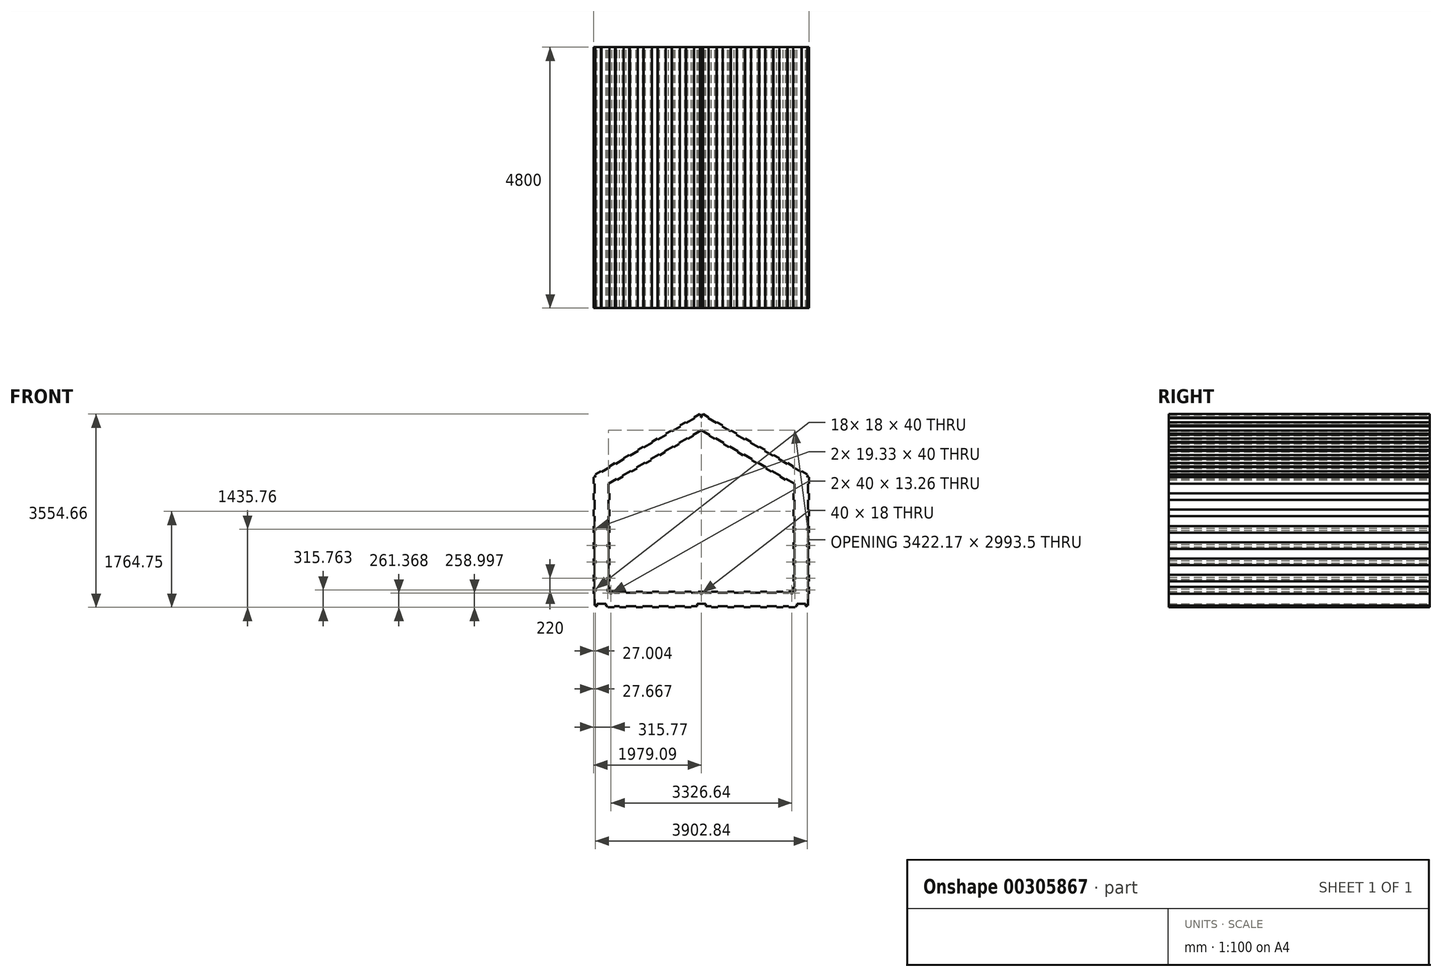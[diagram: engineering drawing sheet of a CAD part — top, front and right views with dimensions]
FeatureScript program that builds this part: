
annotation { "Feature Type Name" : "Feature", "Feature Type Description" : "" }
export const myFeature = defineFeature(function(context is Context, id is Id, definition is map)
    precondition{}
    {
        {
            var Q0;
            Q0=qCreatedBy(makeId("Front.planeOp"),FACE);
            var sketch = newSketch(context, id + "F0", { "sketchPlane" : qUnion([Q0])});
            skLineSegment(sketch, "E0", {"start": v(-89.77, -201.58) * mm, "end": v(-89.77, -291.34) * mm});
            skLineSegment(sketch, "E1", {"start": v(-89.77, -291.34) * mm, "end": v(0, -291.34) * mm});
            skLineSegment(sketch, "E2", {"start": v(0, -291.34) * mm, "end": v(0, -309.34) * mm});
            skLineSegment(sketch, "E3", {"start": v(0, -309.34) * mm, "end": v(100, -309.34) * mm});
            skLineSegment(sketch, "E4", {"start": v(100, -309.34) * mm, "end": v(100, -291.34) * mm});
            skLineSegment(sketch, "E5", {"start": v(100, -291.34) * mm, "end": v(220, -291.34) * mm});
            skLineSegment(sketch, "E6", {"start": v(220, -291.34) * mm, "end": v(220, -309.34) * mm});
            skLineSegment(sketch, "E7", {"start": v(220, -309.34) * mm, "end": v(400, -309.34) * mm});
            skLineSegment(sketch, "E8", {"start": v(400, -309.34) * mm, "end": v(400, -291.34) * mm});
            skLineSegment(sketch, "E9", {"start": v(400, -291.34) * mm, "end": v(520, -291.34) * mm});
            skLineSegment(sketch, "E10", {"start": v(520, -291.34) * mm, "end": v(520, -309.34) * mm});
            skLineSegment(sketch, "E11", {"start": v(520, -309.34) * mm, "end": v(700, -309.34) * mm});
            skLineSegment(sketch, "E12", {"start": v(700, -309.34) * mm, "end": v(700, -291.34) * mm});
            skLineSegment(sketch, "E13", {"start": v(700, -291.34) * mm, "end": v(820, -291.34) * mm});
            skLineSegment(sketch, "E14", {"start": v(820, -291.34) * mm, "end": v(820, -309.34) * mm});
            skLineSegment(sketch, "E15", {"start": v(820, -309.34) * mm, "end": v(1000, -309.34) * mm});
            skLineSegment(sketch, "E16", {"start": v(1000, -309.34) * mm, "end": v(1000, -291.34) * mm});
            skLineSegment(sketch, "E17", {"start": v(1000, -291.34) * mm, "end": v(1120, -291.34) * mm});
            skLineSegment(sketch, "E18", {"start": v(1120, -291.34) * mm, "end": v(1120, -309.34) * mm});
            skLineSegment(sketch, "E19", {"start": v(1120, -309.34) * mm, "end": v(1300, -309.34) * mm});
            skLineSegment(sketch, "E20", {"start": v(1300, -309.34) * mm, "end": v(1300, -291.34) * mm});
            skLineSegment(sketch, "E21", {"start": v(1300, -291.34) * mm, "end": v(1420, -291.34) * mm});
            skLineSegment(sketch, "E22", {"start": v(1420, -291.34) * mm, "end": v(1420, -309.34) * mm});
            skLineSegment(sketch, "E23", {"start": v(1420, -309.34) * mm, "end": v(1543.32, -309.34) * mm});
            skLineSegment(sketch, "E24", {"start": v(1543.32, -309.34) * mm, "end": v(1543.32, -291.34) * mm});
            skLineSegment(sketch, "E25", {"start": v(1543.32, -291.34) * mm, "end": v(1603.32, -291.34) * mm});
            skLineSegment(sketch, "E26.bottom", {"start": v(1583.32, -309.34) * mm, "end": v(1603.32, -309.34) * mm});
            skLineSegment(sketch, "E26.top", {"start": v(1583.32, -327.34) * mm, "end": v(1603.32, -327.34) * mm});
            skLineSegment(sketch, "E26.left", {"start": v(1583.32, -309.34) * mm, "end": v(1583.32, -327.34) * mm});
            skLineSegment(sketch, "E26.right", {"start": v(1603.32, -309.34) * mm, "end": v(1603.32, -327.34) * mm});
            skLineSegment(sketch, "E27", {"start": v(-89.77, -201.58) * mm, "end": v(-107.77, -201.58) * mm});
            skLineSegment(sketch, "E28", {"start": v(-107.77, -201.58) * mm, "end": v(-107.77, -101.58) * mm});
            skLineSegment(sketch, "E29", {"start": v(-107.77, -101.58) * mm, "end": v(-89.77, -101.58) * mm});
            skLineSegment(sketch, "E30", {"start": v(-89.77, -101.58) * mm, "end": v(-89.77, 18.42) * mm});
            skLineSegment(sketch, "E31", {"start": v(-89.77, 18.42) * mm, "end": v(-107.77, 18.42) * mm});
            skLineSegment(sketch, "E32", {"start": v(-107.77, 18.42) * mm, "end": v(-107.77, 198.42) * mm});
            skLineSegment(sketch, "E33", {"start": v(-107.77, 198.42) * mm, "end": v(-89.77, 198.42) * mm});
            skLineSegment(sketch, "E34", {"start": v(-89.77, 198.42) * mm, "end": v(-89.77, 318.42) * mm});
            skLineSegment(sketch, "E35", {"start": v(-89.77, 318.42) * mm, "end": v(-107.77, 318.42) * mm});
            skLineSegment(sketch, "E36", {"start": v(-107.77, 318.42) * mm, "end": v(-107.77, 498.42) * mm});
            skLineSegment(sketch, "E37.bottom", {"start": v(-107.77, -241.58) * mm, "end": v(-125.77, -241.58) * mm});
            skLineSegment(sketch, "E37.top", {"start": v(-107.77, -281.58) * mm, "end": v(-125.77, -281.58) * mm});
            skLineSegment(sketch, "E37.left", {"start": v(-107.77, -241.58) * mm, "end": v(-107.77, -281.58) * mm});
            skLineSegment(sketch, "E37.right", {"start": v(-125.77, -241.58) * mm, "end": v(-125.77, -281.58) * mm});
            skLineSegment(sketch, "E38.bottom", {"start": v(-40, -309.34) * mm, "end": v(-80, -309.34) * mm});
            skLineSegment(sketch, "E38.top", {"start": v(-40, -322.6) * mm, "end": v(-80, -322.6) * mm});
            skLineSegment(sketch, "E38.left", {"start": v(-40, -309.34) * mm, "end": v(-40, -322.6) * mm});
            skLineSegment(sketch, "E38.right", {"start": v(-80, -309.34) * mm, "end": v(-80, -322.6) * mm});
            skLineSegment(sketch, "E39", {"start": v(-107.77, -201.58) * mm, "end": v(-357.77, -201.58) * mm, "construction": true});
            skLineSegment(sketch, "E40", {"start": v(-357.77, -201.58) * mm, "end": v(-375.77, -201.58) * mm});
            skLineSegment(sketch, "E41", {"start": v(-375.77, -201.58) * mm, "end": v(-375.77, -327.35) * mm});
            skLineSegment(sketch, "E42", {"start": v(-357.77, -201.58) * mm, "end": v(-357.77, -101.58) * mm});
            skLineSegment(sketch, "E43", {"start": v(-357.77, -101.58) * mm, "end": v(-375.77, -101.58) * mm});
            skLineSegment(sketch, "E44.bottom", {"start": v(-357.77, -241.58) * mm, "end": v(-339.77, -241.58) * mm});
            skLineSegment(sketch, "E44.top", {"start": v(-357.77, -281.58) * mm, "end": v(-339.77, -281.58) * mm});
            skLineSegment(sketch, "E44.left", {"start": v(-357.77, -241.58) * mm, "end": v(-357.77, -281.58) * mm});
            skLineSegment(sketch, "E44.right", {"start": v(-339.77, -241.58) * mm, "end": v(-339.77, -281.58) * mm});
            skLineSegment(sketch, "E45", {"start": v(-375.77, -101.58) * mm, "end": v(-375.77, 18.42) * mm});
            skLineSegment(sketch, "E46", {"start": v(-375.77, 18.42) * mm, "end": v(-357.77, 18.42) * mm});
            skLineSegment(sketch, "E47.bottom", {"start": v(-357.77, -61.58) * mm, "end": v(-339.77, -61.58) * mm});
            skLineSegment(sketch, "E47.top", {"start": v(-357.77, -21.58) * mm, "end": v(-339.77, -21.58) * mm});
            skLineSegment(sketch, "E47.left", {"start": v(-357.77, -61.58) * mm, "end": v(-357.77, -21.58) * mm});
            skLineSegment(sketch, "E47.right", {"start": v(-339.77, -61.58) * mm, "end": v(-339.77, -21.58) * mm});
            skLineSegment(sketch, "E48", {"start": v(-357.77, 18.42) * mm, "end": v(-357.77, 198.42) * mm});
            skLineSegment(sketch, "E49", {"start": v(-357.77, 198.42) * mm, "end": v(-375.77, 198.42) * mm});
            skLineSegment(sketch, "E50.bottom", {"start": v(-107.77, -21.58) * mm, "end": v(-125.77, -21.58) * mm});
            skLineSegment(sketch, "E50.top", {"start": v(-107.77, -61.58) * mm, "end": v(-125.77, -61.58) * mm});
            skLineSegment(sketch, "E50.left", {"start": v(-107.77, -21.58) * mm, "end": v(-107.77, -61.58) * mm});
            skLineSegment(sketch, "E50.right", {"start": v(-125.77, -21.58) * mm, "end": v(-125.77, -61.58) * mm});
            skLineSegment(sketch, "E51", {"start": v(-375.77, 198.42) * mm, "end": v(-375.77, 318.42) * mm});
            skLineSegment(sketch, "E52", {"start": v(-375.77, 318.42) * mm, "end": v(-357.77, 318.42) * mm});
            skLineSegment(sketch, "E53", {"start": v(-357.77, 318.42) * mm, "end": v(-357.77, 498.42) * mm});
            skLineSegment(sketch, "E54.bottom", {"start": v(-357.77, 238.42) * mm, "end": v(-339.77, 238.42) * mm});
            skLineSegment(sketch, "E54.top", {"start": v(-357.77, 278.42) * mm, "end": v(-339.77, 278.42) * mm});
            skLineSegment(sketch, "E54.left", {"start": v(-357.77, 238.42) * mm, "end": v(-357.77, 278.42) * mm});
            skLineSegment(sketch, "E54.right", {"start": v(-339.77, 238.42) * mm, "end": v(-339.77, 278.42) * mm});
            skLineSegment(sketch, "E55.bottom", {"start": v(-107.77, 238.42) * mm, "end": v(-125.77, 238.42) * mm});
            skLineSegment(sketch, "E55.top", {"start": v(-107.77, 278.42) * mm, "end": v(-125.77, 278.42) * mm});
            skLineSegment(sketch, "E55.left", {"start": v(-107.77, 238.42) * mm, "end": v(-107.77, 278.42) * mm});
            skLineSegment(sketch, "E55.right", {"start": v(-125.77, 238.42) * mm, "end": v(-125.77, 278.42) * mm});
            skLineSegment(sketch, "E56", {"start": v(-357.77, 498.42) * mm, "end": v(-375.77, 498.42) * mm});
            skLineSegment(sketch, "E57", {"start": v(-375.77, 498.42) * mm, "end": v(-375.77, 618.42) * mm});
            skLineSegment(sketch, "E58", {"start": v(-107.77, 498.42) * mm, "end": v(-89.77, 498.42) * mm});
            skLineSegment(sketch, "E59", {"start": v(-89.77, 498.42) * mm, "end": v(-89.77, 618.42) * mm});
            skLineSegment(sketch, "E60.bottom", {"start": v(-357.77, 538.42) * mm, "end": v(-339.77, 538.42) * mm});
            skLineSegment(sketch, "E60.top", {"start": v(-357.77, 578.42) * mm, "end": v(-339.77, 578.42) * mm});
            skLineSegment(sketch, "E60.left", {"start": v(-357.77, 538.42) * mm, "end": v(-357.77, 578.42) * mm});
            skLineSegment(sketch, "E60.right", {"start": v(-339.77, 538.42) * mm, "end": v(-339.77, 578.42) * mm});
            skLineSegment(sketch, "E61.bottom", {"start": v(-107.77, 538.42) * mm, "end": v(-125.77, 538.42) * mm});
            skLineSegment(sketch, "E61.top", {"start": v(-107.77, 578.42) * mm, "end": v(-125.77, 578.42) * mm});
            skLineSegment(sketch, "E61.left", {"start": v(-107.77, 538.42) * mm, "end": v(-107.77, 578.42) * mm});
            skLineSegment(sketch, "E61.right", {"start": v(-125.77, 538.42) * mm, "end": v(-125.77, 578.42) * mm});
            skLineSegment(sketch, "E62", {"start": v(-375.77, 618.42) * mm, "end": v(-357.77, 618.42) * mm});
            skPoint(sketch, "E62.endSnap0", {"position": v(-357.77, 558.42) * mm});
            skLineSegment(sketch, "E63", {"start": v(-89.77, 618.42) * mm, "end": v(-107.77, 618.42) * mm});
            skPoint(sketch, "E63.endSnap0", {"position": v(-107.77, 558.42) * mm});
            skLineSegment(sketch, "E64", {"start": v(-357.77, 618.42) * mm, "end": v(-357.77, 798.42) * mm});
            skLineSegment(sketch, "E65", {"start": v(-107.77, 618.42) * mm, "end": v(-107.77, 798.42) * mm});
            skLineSegment(sketch, "E66", {"start": v(-107.77, 798.42) * mm, "end": v(-89.77, 798.42) * mm});
            skLineSegment(sketch, "E67", {"start": v(-89.77, 798.42) * mm, "end": v(-89.77, 918.42) * mm});
            skLineSegment(sketch, "E68", {"start": v(-89.77, 918.42) * mm, "end": v(-107.77, 918.42) * mm});
            skLineSegment(sketch, "E69", {"start": v(-107.77, 918.42) * mm, "end": v(-107.77, 1098.42) * mm});
            skLineSegment(sketch, "E70", {"start": v(-357.77, 798.42) * mm, "end": v(-375.77, 798.42) * mm});
            skLineSegment(sketch, "E71", {"start": v(-375.77, 798.42) * mm, "end": v(-375.77, 918.42) * mm});
            skLineSegment(sketch, "E72", {"start": v(-375.77, 918.42) * mm, "end": v(-357.77, 918.42) * mm});
            skLineSegment(sketch, "E73", {"start": v(-357.77, 918.42) * mm, "end": v(-357.77, 1098.42) * mm});
            skLineSegment(sketch, "E74.bottom", {"start": v(-357.77, 838.42) * mm, "end": v(-338.44, 838.42) * mm});
            skLineSegment(sketch, "E74.top", {"start": v(-357.77, 878.42) * mm, "end": v(-338.44, 878.42) * mm});
            skLineSegment(sketch, "E74.left", {"start": v(-357.77, 838.42) * mm, "end": v(-357.77, 878.42) * mm});
            skLineSegment(sketch, "E74.right", {"start": v(-338.44, 838.42) * mm, "end": v(-338.44, 878.42) * mm});
            skLineSegment(sketch, "E75.bottom", {"start": v(-107.77, 838.42) * mm, "end": v(-125.77, 838.42) * mm});
            skLineSegment(sketch, "E75.top", {"start": v(-107.77, 878.42) * mm, "end": v(-125.77, 878.42) * mm});
            skLineSegment(sketch, "E75.left", {"start": v(-107.77, 838.42) * mm, "end": v(-107.77, 878.42) * mm});
            skLineSegment(sketch, "E75.right", {"start": v(-125.77, 838.42) * mm, "end": v(-125.77, 878.42) * mm});
            skLineSegment(sketch, "E76", {"start": v(-357.77, 1098.42) * mm, "end": v(-375.77, 1098.42) * mm});
            skLineSegment(sketch, "E77", {"start": v(-375.77, 1098.42) * mm, "end": v(-375.77, 1218.42) * mm});
            skLineSegment(sketch, "E78", {"start": v(-107.77, 1098.42) * mm, "end": v(-89.77, 1098.42) * mm});
            skLineSegment(sketch, "E79", {"start": v(-89.77, 1098.42) * mm, "end": v(-89.77, 1218.42) * mm});
            skLineSegment(sketch, "E80", {"start": v(-375.77, 1218.42) * mm, "end": v(-357.77, 1218.42) * mm});
            skLineSegment(sketch, "E81", {"start": v(-357.77, 1218.42) * mm, "end": v(-357.77, 1398.42) * mm});
            skLineSegment(sketch, "E82", {"start": v(-89.77, 1218.42) * mm, "end": v(-107.77, 1218.42) * mm});
            skLineSegment(sketch, "E83", {"start": v(-107.77, 1218.42) * mm, "end": v(-107.77, 1398.42) * mm});
            skLineSegment(sketch, "E84", {"start": v(-357.77, 1398.42) * mm, "end": v(-375.77, 1398.42) * mm});
            skLineSegment(sketch, "E85", {"start": v(-375.77, 1398.42) * mm, "end": v(-375.77, 1518.42) * mm});
            skLineSegment(sketch, "E86", {"start": v(-375.77, 1518.42) * mm, "end": v(-357.77, 1518.42) * mm});
            skLineSegment(sketch, "E87", {"start": v(-107.77, 1398.42) * mm, "end": v(-89.77, 1398.42) * mm});
            skLineSegment(sketch, "E88", {"start": v(-89.77, 1398.42) * mm, "end": v(-89.77, 1518.42) * mm});
            skLineSegment(sketch, "E89", {"start": v(-89.77, 1518.42) * mm, "end": v(-107.77, 1518.42) * mm});
            skLineSegment(sketch, "E90", {"start": v(-357.77, 1518.42) * mm, "end": v(-357.77, 1698.42) * mm});
            skLineSegment(sketch, "E91", {"start": v(-357.77, 1698.42) * mm, "end": v(-375.77, 1698.42) * mm});
            skLineSegment(sketch, "E92", {"start": v(-375.77, 1698.42) * mm, "end": v(-375.77, 1818.42) * mm});
            skLineSegment(sketch, "E93", {"start": v(-375.77, 1818.42) * mm, "end": v(-357.77, 1818.42) * mm});
            skLineSegment(sketch, "E94", {"start": v(-357.77, 1818.42) * mm, "end": v(-357.77, 1840.65) * mm});
            skLineSegment(sketch, "E95", {"start": v(-357.77, 1818.42) * mm, "end": v(-338.51, 1851.77) * mm});
            skLineSegment(sketch, "E96", {"start": v(-357.77, 1840.65) * mm, "end": v(-338.51, 1851.77) * mm});
            skLineSegment(sketch, "E97", {"start": v(-338.51, 1851.77) * mm, "end": v(-347.51, 1867.36) * mm});
            skLineSegment(sketch, "E98", {"start": v(-347.51, 1867.36) * mm, "end": v(-243.59, 1927.35) * mm});
            skLineSegment(sketch, "E99", {"start": v(-243.59, 1927.35) * mm, "end": v(-234.59, 1911.77) * mm});
            skLineSegment(sketch, "E100", {"start": v(-234.59, 1911.77) * mm, "end": v(-78.7, 2001.76) * mm});
            skLineSegment(sketch, "E101", {"start": v(-78.7, 2001.76) * mm, "end": v(-87.7, 2017.35) * mm});
            skLineSegment(sketch, "E102", {"start": v(-87.7, 2017.35) * mm, "end": v(16.22, 2077.35) * mm});
            skLineSegment(sketch, "E103", {"start": v(16.22, 2077.35) * mm, "end": v(25.22, 2061.76) * mm});
            skLineSegment(sketch, "E104", {"start": v(-78.7, 2001.76) * mm, "end": v(46.3, 1785.25) * mm, "construction": true});
            skLineSegment(sketch, "E105", {"start": v(46.3, 1785.25) * mm, "end": v(55.3, 1769.67) * mm});
            skLineSegment(sketch, "E106", {"start": v(55.3, 1769.67) * mm, "end": v(159.22, 1829.66) * mm});
            skLineSegment(sketch, "E107", {"start": v(159.22, 1829.66) * mm, "end": v(150.22, 1845.25) * mm});
            skLineSegment(sketch, "E108", {"start": v(-107.77, 1518.42) * mm, "end": v(-107.77, 1696.31) * mm});
            skLineSegment(sketch, "E109", {"start": v(46.3, 1785.25) * mm, "end": v(-107.77, 1696.31) * mm});
            skLineSegment(sketch, "E110", {"start": v(25.22, 2061.76) * mm, "end": v(181.1, 2151.76) * mm});
            skLineSegment(sketch, "E111", {"start": v(150.22, 1845.25) * mm, "end": v(306.1, 1935.25) * mm});
            skLineSegment(sketch, "E112", {"start": v(181.1, 2151.76) * mm, "end": v(172.11, 2167.35) * mm});
            skLineSegment(sketch, "E113", {"start": v(172.11, 2167.35) * mm, "end": v(276.03, 2227.34) * mm});
            skLineSegment(sketch, "E114", {"start": v(306.1, 1935.25) * mm, "end": v(315.1, 1919.66) * mm});
            skLineSegment(sketch, "E115", {"start": v(315.1, 1919.66) * mm, "end": v(419.03, 1979.66) * mm});
            skLineSegment(sketch, "E116", {"start": v(419.03, 1979.66) * mm, "end": v(410.03, 1995.25) * mm});
            skLineSegment(sketch, "E117", {"start": v(410.03, 1995.25) * mm, "end": v(565.92, 2085.24) * mm});
            skLineSegment(sketch, "E118", {"start": v(276.03, 2227.34) * mm, "end": v(285.03, 2211.76) * mm});
            skLineSegment(sketch, "E119", {"start": v(285.03, 2211.76) * mm, "end": v(440.92, 2301.75) * mm});
            skLineSegment(sketch, "E120", {"start": v(440.92, 2301.75) * mm, "end": v(431.92, 2317.34) * mm});
            skLineSegment(sketch, "E121", {"start": v(431.92, 2317.34) * mm, "end": v(535.84, 2377.34) * mm});
            skLineSegment(sketch, "E122", {"start": v(565.92, 2085.24) * mm, "end": v(574.92, 2069.66) * mm});
            skLineSegment(sketch, "E123", {"start": v(574.92, 2069.66) * mm, "end": v(678.84, 2129.65) * mm});
            skLineSegment(sketch, "E124", {"start": v(535.84, 2377.34) * mm, "end": v(544.84, 2361.75) * mm});
            skLineSegment(sketch, "E125", {"start": v(544.84, 2361.75) * mm, "end": v(700.73, 2451.75) * mm});
            skLineSegment(sketch, "E126", {"start": v(678.84, 2129.65) * mm, "end": v(669.84, 2145.24) * mm});
            skLineSegment(sketch, "E127", {"start": v(669.84, 2145.24) * mm, "end": v(825.73, 2235.24) * mm});
            skLineSegment(sketch, "E128", {"start": v(700.73, 2451.75) * mm, "end": v(691.73, 2467.34) * mm});
            skLineSegment(sketch, "E129", {"start": v(691.73, 2467.34) * mm, "end": v(795.66, 2527.33) * mm});
            skLineSegment(sketch, "E130", {"start": v(825.73, 2235.24) * mm, "end": v(834.73, 2219.65) * mm});
            skLineSegment(sketch, "E131", {"start": v(834.73, 2219.65) * mm, "end": v(938.65, 2279.65) * mm});
            skLineSegment(sketch, "E132", {"start": v(795.66, 2527.33) * mm, "end": v(804.66, 2511.75) * mm});
            skLineSegment(sketch, "E133", {"start": v(804.66, 2511.75) * mm, "end": v(960.54, 2601.74) * mm});
            skLineSegment(sketch, "E134", {"start": v(960.54, 2601.74) * mm, "end": v(951.54, 2617.33) * mm});
            skLineSegment(sketch, "E135", {"start": v(951.54, 2617.33) * mm, "end": v(1055.47, 2677.33) * mm});
            skLineSegment(sketch, "E136", {"start": v(1055.47, 2677.33) * mm, "end": v(1064.47, 2661.74) * mm});
            skLineSegment(sketch, "E137", {"start": v(1064.47, 2661.74) * mm, "end": v(1220.35, 2751.74) * mm});
            skLineSegment(sketch, "E138", {"start": v(1220.35, 2751.74) * mm, "end": v(1211.35, 2767.33) * mm});
            skLineSegment(sketch, "E139", {"start": v(1211.35, 2767.33) * mm, "end": v(1315.28, 2827.32) * mm});
            skLineSegment(sketch, "E140", {"start": v(1315.28, 2827.32) * mm, "end": v(1324.28, 2811.74) * mm});
            skLineSegment(sketch, "E141", {"start": v(1324.28, 2811.74) * mm, "end": v(1480.16, 2901.73) * mm});
            skLineSegment(sketch, "E142", {"start": v(1480.16, 2901.73) * mm, "end": v(1471.16, 2917.32) * mm});
            skLineSegment(sketch, "E143", {"start": v(1471.16, 2917.32) * mm, "end": v(1575.09, 2977.32) * mm});
            skLineSegment(sketch, "E144", {"start": v(938.65, 2279.65) * mm, "end": v(929.65, 2295.24) * mm});
            skLineSegment(sketch, "E145", {"start": v(929.65, 2295.24) * mm, "end": v(1085.54, 2385.23) * mm});
            skLineSegment(sketch, "E146", {"start": v(1085.54, 2385.23) * mm, "end": v(1094.54, 2369.64) * mm});
            skLineSegment(sketch, "E147", {"start": v(1094.54, 2369.64) * mm, "end": v(1198.46, 2429.64) * mm});
            skLineSegment(sketch, "E148", {"start": v(1198.46, 2429.64) * mm, "end": v(1189.46, 2445.23) * mm});
            skLineSegment(sketch, "E149", {"start": v(1189.46, 2445.23) * mm, "end": v(1345.35, 2535.23) * mm});
            skLineSegment(sketch, "E150", {"start": v(1345.35, 2535.23) * mm, "end": v(1354.35, 2519.64) * mm});
            skLineSegment(sketch, "E151", {"start": v(1354.35, 2519.64) * mm, "end": v(1458.27, 2579.64) * mm});
            skLineSegment(sketch, "E152", {"start": v(1458.27, 2579.64) * mm, "end": v(1449.27, 2595.23) * mm});
            skLineSegment(sketch, "E153", {"start": v(1449.27, 2595.23) * mm, "end": v(1603.33, 2684.17) * mm});
            skLineSegment(sketch, "E154", {"start": v(1575.09, 2977.32) * mm, "end": v(1584.09, 2961.73) * mm});
            skLineSegment(sketch, "E155", {"start": v(1584.09, 2961.73) * mm, "end": v(1594.33, 2967.65) * mm});
            skLineSegment(sketch, "E156", {"start": v(1594.33, 2967.65) * mm, "end": v(1594.33, 2917.65) * mm});
            skLineSegment(sketch, "E157", {"start": v(1594.33, 2917.65) * mm, "end": v(1603.33, 2917.65) * mm});
            skLineSegment(sketch, "E158", {"start": v(960.54, 2601.74) * mm, "end": v(1085.54, 2385.23) * mm, "construction": true});
            skLineSegment(sketch, "E159", {"start": v(1420, -559.34) * mm, "end": v(1420, -577.34) * mm});
            skLineSegment(sketch, "E160", {"start": v(1420, -577.34) * mm, "end": v(1300, -577.34) * mm});
            skLineSegment(sketch, "E161", {"start": v(1300, -577.34) * mm, "end": v(1300, -559.34) * mm});
            skLineSegment(sketch, "E162", {"start": v(1300, -559.34) * mm, "end": v(1120, -559.34) * mm});
            skLineSegment(sketch, "E163", {"start": v(1120, -559.34) * mm, "end": v(1120, -577.34) * mm});
            skLineSegment(sketch, "E164", {"start": v(1120, -577.34) * mm, "end": v(1000, -577.34) * mm});
            skLineSegment(sketch, "E165", {"start": v(1000, -577.34) * mm, "end": v(1000, -559.34) * mm});
            skLineSegment(sketch, "E166", {"start": v(1000, -559.34) * mm, "end": v(820, -559.34) * mm});
            skLineSegment(sketch, "E167", {"start": v(820, -559.34) * mm, "end": v(820, -577.34) * mm});
            skLineSegment(sketch, "E168", {"start": v(820, -577.34) * mm, "end": v(700, -577.34) * mm});
            skLineSegment(sketch, "E169", {"start": v(700, -577.34) * mm, "end": v(700, -559.34) * mm});
            skLineSegment(sketch, "E170", {"start": v(700, -559.34) * mm, "end": v(520, -559.34) * mm});
            skLineSegment(sketch, "E171", {"start": v(520, -559.34) * mm, "end": v(520, -577.34) * mm});
            skLineSegment(sketch, "E172", {"start": v(520, -577.34) * mm, "end": v(400, -577.34) * mm});
            skLineSegment(sketch, "E173", {"start": v(400, -577.34) * mm, "end": v(400, -559.34) * mm});
            skLineSegment(sketch, "E174", {"start": v(400, -559.34) * mm, "end": v(220, -559.34) * mm});
            skLineSegment(sketch, "E175", {"start": v(220, -559.34) * mm, "end": v(220, -577.34) * mm});
            skLineSegment(sketch, "E176", {"start": v(220, -577.34) * mm, "end": v(100, -577.34) * mm});
            skLineSegment(sketch, "E177", {"start": v(100, -577.34) * mm, "end": v(100, -559.34) * mm});
            skLineSegment(sketch, "E178", {"start": v(100, -559.34) * mm, "end": v(0, -559.34) * mm});
            skLineSegment(sketch, "E179", {"start": v(0, -559.34) * mm, "end": v(0, -577.34) * mm});
            skLineSegment(sketch, "E180", {"start": v(0, -577.34) * mm, "end": v(-120, -577.34) * mm});
            skLineSegment(sketch, "E181", {"start": v(-120, -577.34) * mm, "end": v(-120, -559.34) * mm});
            skLineSegment(sketch, "E182", {"start": v(-120, -559.34) * mm, "end": v(-152.77, -559.34) * mm});
            skLineSegment(sketch, "E183", {"start": v(-152.77, -559.34) * mm, "end": v(-152.77, -509.34) * mm});
            skLineSegment(sketch, "E184", {"start": v(-152.77, -509.34) * mm, "end": v(-312.77, -509.34) * mm});
            skLineSegment(sketch, "E185", {"start": v(-312.77, -509.34) * mm, "end": v(-312.77, -559.34) * mm});
            skLineSegment(sketch, "E186", {"start": v(-312.77, -559.34) * mm, "end": v(-337.77, -559.34) * mm});
            skLineSegment(sketch, "E187", {"start": v(-337.77, -559.34) * mm, "end": v(-337.77, -541.34) * mm});
            skLineSegment(sketch, "E188", {"start": v(-337.77, -541.34) * mm, "end": v(-357.77, -541.34) * mm});
            skLineSegment(sketch, "E189", {"start": v(-357.77, -541.34) * mm, "end": v(-357.77, -327.35) * mm});
            skLineSegment(sketch, "E190", {"start": v(-357.77, -327.35) * mm, "end": v(-375.77, -327.35) * mm});
            skLineSegment(sketch, "E191", {"start": v(1603.32, -816.57) * mm, "end": v(1603.32, 3183.43) * mm, "construction": true});
            skLineSegment(sketch, "E192", {"start": v(1420, -559.34) * mm, "end": v(1523.32, -559.34) * mm});
            skLineSegment(sketch, "E193", {"start": v(1523.32, -559.34) * mm, "end": v(1523.32, -509.34) * mm});
            skLineSegment(sketch, "E194", {"start": v(1523.32, -509.34) * mm, "end": v(1603.32, -509.34) * mm});
            skLineSegment(sketch, "E195.MirrorCS", {"start": v(3564.4, 578.42) * mm, "end": v(3546.4, 578.42) * mm});
            skLineSegment(sketch, "E196.MirrorCS", {"start": v(3564.4, 1840.65) * mm, "end": v(3545.15, 1851.77) * mm});
            skLineSegment(sketch, "E197.MirrorCS", {"start": v(3564.4, 538.42) * mm, "end": v(3546.4, 538.42) * mm});
            skLineSegment(sketch, "E198.MirrorCS", {"start": v(3314.4, 578.42) * mm, "end": v(3332.4, 578.42) * mm});
            skLineSegment(sketch, "E199.MirrorCS", {"start": v(3582.4, 1818.42) * mm, "end": v(3564.4, 1818.42) * mm});
            skLineSegment(sketch, "E200.MirrorCS", {"start": v(3314.4, 538.42) * mm, "end": v(3332.4, 538.42) * mm});
            skLineSegment(sketch, "E201.MirrorCS", {"start": v(3564.4, 498.42) * mm, "end": v(3582.4, 498.42) * mm});
            skLineSegment(sketch, "E202.MirrorCS", {"start": v(3564.4, 538.42) * mm, "end": v(3564.4, 578.42) * mm});
            skLineSegment(sketch, "E203.MirrorCS", {"start": v(3545.15, 1851.77) * mm, "end": v(3554.15, 1867.36) * mm});
            skLineSegment(sketch, "E204.MirrorCS", {"start": v(3582.4, 618.42) * mm, "end": v(3564.4, 618.42) * mm});
            skLineSegment(sketch, "E205.MirrorCS", {"start": v(3564.4, -61.58) * mm, "end": v(3546.4, -61.58) * mm});
            skLineSegment(sketch, "E206.MirrorCS", {"start": v(3582.4, 498.42) * mm, "end": v(3582.4, 618.42) * mm});
            skLineSegment(sketch, "E207.MirrorCS", {"start": v(1663.32, -309.34) * mm, "end": v(1663.32, -291.34) * mm});
            skLineSegment(sketch, "E208.MirrorCS", {"start": v(3450.22, 1927.35) * mm, "end": v(3441.22, 1911.77) * mm});
            skLineSegment(sketch, "E209.MirrorCS", {"start": v(3546.4, 538.42) * mm, "end": v(3546.4, 578.42) * mm});
            skLineSegment(sketch, "E210.MirrorCS", {"start": v(3314.4, 498.42) * mm, "end": v(3296.4, 498.42) * mm});
            skLineSegment(sketch, "E211.MirrorCS", {"start": v(3554.15, 1867.36) * mm, "end": v(3450.22, 1927.35) * mm});
            skLineSegment(sketch, "E212.MirrorCS", {"start": v(3564.4, -281.58) * mm, "end": v(3546.4, -281.58) * mm});
            skLineSegment(sketch, "E213.MirrorCS", {"start": v(3564.4, -241.58) * mm, "end": v(3546.4, -241.58) * mm});
            skLineSegment(sketch, "E214.MirrorCS", {"start": v(3564.4, -21.58) * mm, "end": v(3546.4, -21.58) * mm});
            skLineSegment(sketch, "E215.MirrorCS", {"start": v(3296.4, 618.42) * mm, "end": v(3314.4, 618.42) * mm});
            skLineSegment(sketch, "E216.MirrorCS", {"start": v(3564.4, -61.58) * mm, "end": v(3564.4, -21.58) * mm});
            skLineSegment(sketch, "E217.MirrorCS", {"start": v(3332.4, 538.42) * mm, "end": v(3332.4, 578.42) * mm});
            skLineSegment(sketch, "E218.MirrorCS", {"start": v(1623.32, -327.34) * mm, "end": v(1603.32, -327.34) * mm});
            skLineSegment(sketch, "E219.MirrorCS", {"start": v(3564.4, 1818.42) * mm, "end": v(3564.4, 1840.65) * mm});
            skLineSegment(sketch, "E220.MirrorCS", {"start": v(3564.4, 1818.42) * mm, "end": v(3545.15, 1851.77) * mm});
            skLineSegment(sketch, "E221.MirrorCS", {"start": v(3296.4, 498.42) * mm, "end": v(3296.4, 618.42) * mm});
            skLineSegment(sketch, "E222.MirrorCS", {"start": v(3314.4, 538.42) * mm, "end": v(3314.4, 578.42) * mm});
            skLineSegment(sketch, "E223.MirrorCS", {"start": v(1623.32, -309.34) * mm, "end": v(1603.32, -309.34) * mm});
            skLineSegment(sketch, "E224.MirrorCS", {"start": v(3564.4, 278.42) * mm, "end": v(3546.4, 278.42) * mm});
            skLineSegment(sketch, "E225.MirrorCS", {"start": v(3564.4, 878.42) * mm, "end": v(3545.08, 878.42) * mm});
            skLineSegment(sketch, "E226.MirrorCS", {"start": v(1663.32, -291.34) * mm, "end": v(1603.32, -291.34) * mm});
            skLineSegment(sketch, "E227.MirrorCS", {"start": v(3314.4, -281.58) * mm, "end": v(3332.4, -281.58) * mm});
            skLineSegment(sketch, "E228.MirrorCS", {"start": v(3582.4, -101.58) * mm, "end": v(3582.4, 18.42) * mm});
            skLineSegment(sketch, "E229.MirrorCS", {"start": v(3564.4, -201.58) * mm, "end": v(3582.4, -201.58) * mm});
            skLineSegment(sketch, "E230.MirrorCS", {"start": v(3564.4, 238.42) * mm, "end": v(3546.4, 238.42) * mm});
            skLineSegment(sketch, "E231.MirrorCS", {"start": v(3564.4, 838.42) * mm, "end": v(3545.08, 838.42) * mm});
            skLineSegment(sketch, "E232.MirrorCS", {"start": v(3314.4, -241.58) * mm, "end": v(3332.4, -241.58) * mm});
            skLineSegment(sketch, "E233.MirrorCS", {"start": v(3564.4, -241.58) * mm, "end": v(3564.4, -281.58) * mm});
            skLineSegment(sketch, "E234.MirrorCS", {"start": v(3286.64, -309.34) * mm, "end": v(3286.64, -322.6) * mm});
            skLineSegment(sketch, "E235.MirrorCS", {"start": v(3296.4, -201.58) * mm, "end": v(3314.4, -201.58) * mm});
            skLineSegment(sketch, "E236.MirrorCS", {"start": v(3546.4, -61.58) * mm, "end": v(3546.4, -21.58) * mm});
            skLineSegment(sketch, "E237.MirrorCS", {"start": v(1623.32, -309.34) * mm, "end": v(1623.32, -327.34) * mm});
            skLineSegment(sketch, "E238.MirrorCS", {"start": v(3246.64, -322.6) * mm, "end": v(3286.64, -322.6) * mm});
            skLineSegment(sketch, "E239.MirrorCS", {"start": v(3332.4, -21.58) * mm, "end": v(3332.4, -61.58) * mm});
            skLineSegment(sketch, "E240.MirrorCS", {"start": v(3564.4, -101.58) * mm, "end": v(3582.4, -101.58) * mm});
            skLineSegment(sketch, "E241.MirrorCS", {"start": v(3564.4, -201.58) * mm, "end": v(3564.4, -101.58) * mm});
            skLineSegment(sketch, "E242.MirrorCS", {"start": v(3314.4, -21.58) * mm, "end": v(3314.4, -61.58) * mm});
            skLineSegment(sketch, "E243.MirrorCS", {"start": v(3582.4, 18.42) * mm, "end": v(3564.4, 18.42) * mm});
            skLineSegment(sketch, "E244.MirrorCS", {"start": v(3296.4, 18.42) * mm, "end": v(3314.4, 18.42) * mm});
            skLineSegment(sketch, "E245.MirrorCS", {"start": v(3564.4, -327.35) * mm, "end": v(3582.4, -327.35) * mm});
            skLineSegment(sketch, "E246.MirrorCS", {"start": v(3296.4, -101.58) * mm, "end": v(3296.4, 18.42) * mm});
            skLineSegment(sketch, "E247.MirrorCS", {"start": v(3314.4, -21.58) * mm, "end": v(3332.4, -21.58) * mm});
            skLineSegment(sketch, "E248.MirrorCS", {"start": v(3314.4, -101.58) * mm, "end": v(3296.4, -101.58) * mm});
            skLineSegment(sketch, "E249.MirrorCS", {"start": v(3546.4, -241.58) * mm, "end": v(3546.4, -281.58) * mm});
            skLineSegment(sketch, "E250.MirrorCS", {"start": v(3314.4, -201.58) * mm, "end": v(3564.4, -201.58) * mm, "construction": true});
            skLineSegment(sketch, "E251.MirrorCS", {"start": v(3314.4, -61.58) * mm, "end": v(3332.4, -61.58) * mm});
            skLineSegment(sketch, "E252.MirrorCS", {"start": v(3206.64, -291.34) * mm, "end": v(3206.64, -309.34) * mm});
            skLineSegment(sketch, "E253.MirrorCS", {"start": v(3296.4, -291.34) * mm, "end": v(3206.64, -291.34) * mm});
            skLineSegment(sketch, "E254.MirrorCS", {"start": v(3296.4, -201.58) * mm, "end": v(3296.4, -291.34) * mm});
            skLineSegment(sketch, "E255.MirrorCS", {"start": v(3314.4, -201.58) * mm, "end": v(3314.4, -101.58) * mm});
            skLineSegment(sketch, "E256.MirrorCS", {"start": v(3582.4, 318.42) * mm, "end": v(3564.4, 318.42) * mm});
            skLineSegment(sketch, "E257.MirrorCS", {"start": v(3246.64, -309.34) * mm, "end": v(3246.64, -322.6) * mm});
            skLineSegment(sketch, "E258.MirrorCS", {"start": v(3314.4, 838.42) * mm, "end": v(3332.4, 838.42) * mm});
            skLineSegment(sketch, "E259.MirrorCS", {"start": v(3246.64, -309.34) * mm, "end": v(3286.64, -309.34) * mm});
            skLineSegment(sketch, "E260.MirrorCS", {"start": v(3314.4, 878.42) * mm, "end": v(3332.4, 878.42) * mm});
            skLineSegment(sketch, "E261.MirrorCS", {"start": v(3564.4, 798.42) * mm, "end": v(3582.4, 798.42) * mm});
            skLineSegment(sketch, "E262.MirrorCS", {"start": v(3332.4, -241.58) * mm, "end": v(3332.4, -281.58) * mm});
            skLineSegment(sketch, "E263.MirrorCS", {"start": v(3564.4, 238.42) * mm, "end": v(3564.4, 278.42) * mm});
            skLineSegment(sketch, "E264.MirrorCS", {"start": v(3564.4, 838.42) * mm, "end": v(3564.4, 878.42) * mm});
            skLineSegment(sketch, "E265.MirrorCS", {"start": v(3314.4, -241.58) * mm, "end": v(3314.4, -281.58) * mm});
            skLineSegment(sketch, "E266.MirrorCS", {"start": v(3582.4, -201.58) * mm, "end": v(3582.4, -327.35) * mm});
            skLineSegment(sketch, "E267.MirrorCS", {"start": v(3296.4, 798.42) * mm, "end": v(3296.4, 918.42) * mm});
            skLineSegment(sketch, "E268.MirrorCS", {"start": v(3564.4, 198.42) * mm, "end": v(3582.4, 198.42) * mm});
            skLineSegment(sketch, "E269.MirrorCS", {"start": v(3564.4, 318.42) * mm, "end": v(3564.4, 498.42) * mm});
            skLineSegment(sketch, "E270.MirrorCS", {"start": v(3544.4, -541.34) * mm, "end": v(3564.4, -541.34) * mm});
            skLineSegment(sketch, "E271.MirrorCS", {"start": v(3314.4, 798.42) * mm, "end": v(3296.4, 798.42) * mm});
            skLineSegment(sketch, "E272.MirrorCS", {"start": v(3206.64, -309.34) * mm, "end": v(3106.64, -309.34) * mm});
            skLineSegment(sketch, "E273.MirrorCS", {"start": v(3314.4, 618.42) * mm, "end": v(3314.4, 798.42) * mm});
            skLineSegment(sketch, "E274.MirrorCS", {"start": v(3332.4, 838.42) * mm, "end": v(3332.4, 878.42) * mm});
            skLineSegment(sketch, "E275.MirrorCS", {"start": v(3564.4, 18.42) * mm, "end": v(3564.4, 198.42) * mm});
            skLineSegment(sketch, "E276.MirrorCS", {"start": v(3582.4, 918.42) * mm, "end": v(3564.4, 918.42) * mm});
            skLineSegment(sketch, "E277.MirrorCS", {"start": v(3296.4, 318.42) * mm, "end": v(3314.4, 318.42) * mm});
            skLineSegment(sketch, "E278.MirrorCS", {"start": v(1631.55, 2977.32) * mm, "end": v(1622.55, 2961.73) * mm});
            skLineSegment(sketch, "E279.MirrorCS", {"start": v(3564.4, 618.42) * mm, "end": v(3564.4, 798.42) * mm});
            skLineSegment(sketch, "E280.MirrorCS", {"start": v(3314.4, 838.42) * mm, "end": v(3314.4, 878.42) * mm});
            skLineSegment(sketch, "E281.MirrorCS", {"start": v(3582.4, 798.42) * mm, "end": v(3582.4, 918.42) * mm});
            skLineSegment(sketch, "E282.MirrorCS", {"start": v(3582.4, 198.42) * mm, "end": v(3582.4, 318.42) * mm});
            skLineSegment(sketch, "E283.MirrorCS", {"start": v(3314.4, 238.42) * mm, "end": v(3332.4, 238.42) * mm});
            skLineSegment(sketch, "E284.MirrorCS", {"start": v(3519.4, -509.34) * mm, "end": v(3519.4, -559.34) * mm});
            skLineSegment(sketch, "E285.MirrorCS", {"start": v(3314.4, 278.42) * mm, "end": v(3332.4, 278.42) * mm});
            skLineSegment(sketch, "E286.MirrorCS", {"start": v(3314.4, 198.42) * mm, "end": v(3296.4, 198.42) * mm});
            skLineSegment(sketch, "E287.MirrorCS", {"start": v(3546.4, 238.42) * mm, "end": v(3546.4, 278.42) * mm});
            skLineSegment(sketch, "E288.MirrorCS", {"start": v(3545.08, 838.42) * mm, "end": v(3545.08, 878.42) * mm});
            skLineSegment(sketch, "E289.MirrorCS", {"start": v(3296.4, 918.42) * mm, "end": v(3314.4, 918.42) * mm});
            skLineSegment(sketch, "E290.MirrorCS", {"start": v(3326.64, -559.34) * mm, "end": v(3359.4, -559.34) * mm});
            skLineSegment(sketch, "E291.MirrorCS", {"start": v(1726.47, 2901.73) * mm, "end": v(1735.47, 2917.32) * mm});
            skLineSegment(sketch, "E292.MirrorCS", {"start": v(3326.64, -577.34) * mm, "end": v(3326.64, -559.34) * mm});
            skLineSegment(sketch, "E293.MirrorCS", {"start": v(3285.34, 2001.76) * mm, "end": v(3294.34, 2017.35) * mm});
            skLineSegment(sketch, "E294.MirrorCS", {"start": v(3206.64, -577.34) * mm, "end": v(3326.64, -577.34) * mm});
            skLineSegment(sketch, "E295.MirrorCS", {"start": v(3564.4, -541.34) * mm, "end": v(3564.4, -327.35) * mm});
            skLineSegment(sketch, "E296.MirrorCS", {"start": v(1612.3, 2917.65) * mm, "end": v(1603.3, 2917.65) * mm});
            skLineSegment(sketch, "E297.MirrorCS", {"start": v(1612.3, 2967.65) * mm, "end": v(1612.3, 2917.65) * mm});
            skLineSegment(sketch, "E298.MirrorCS", {"start": v(3314.4, 318.42) * mm, "end": v(3314.4, 498.42) * mm});
            skLineSegment(sketch, "E299.MirrorCS", {"start": v(3106.64, -309.34) * mm, "end": v(3106.64, -291.34) * mm});
            skLineSegment(sketch, "E300.MirrorCS", {"start": v(3544.4, -559.34) * mm, "end": v(3544.4, -541.34) * mm});
            skLineSegment(sketch, "E301.MirrorCS", {"start": v(1622.55, 2961.73) * mm, "end": v(1612.3, 2967.65) * mm});
            skLineSegment(sketch, "E302.MirrorCS", {"start": v(3332.4, 238.42) * mm, "end": v(3332.4, 278.42) * mm});
            skLineSegment(sketch, "E303.MirrorCS", {"start": v(3519.4, -559.34) * mm, "end": v(3544.4, -559.34) * mm});
            skLineSegment(sketch, "E304.MirrorCS", {"start": v(2640.72, 2085.24) * mm, "end": v(2631.72, 2069.66) * mm});
            skLineSegment(sketch, "E305.MirrorCS", {"start": v(3314.4, 238.42) * mm, "end": v(3314.4, 278.42) * mm});
            skLineSegment(sketch, "E306.MirrorCS", {"start": v(3296.4, 198.42) * mm, "end": v(3296.4, 318.42) * mm});
            skLineSegment(sketch, "E307.MirrorCS", {"start": v(3359.4, -509.34) * mm, "end": v(3519.4, -509.34) * mm});
            skLineSegment(sketch, "E308.MirrorCS", {"start": v(3160.34, 1785.25) * mm, "end": v(3151.34, 1769.67) * mm});
            skLineSegment(sketch, "E309.MirrorCS", {"start": v(3359.4, -559.34) * mm, "end": v(3359.4, -509.34) * mm});
            skLineSegment(sketch, "E310.MirrorCS", {"start": v(1735.47, 2917.32) * mm, "end": v(1631.55, 2977.32) * mm});
            skLineSegment(sketch, "E311.MirrorCS", {"start": v(3314.4, 18.42) * mm, "end": v(3314.4, 198.42) * mm});
            skLineSegment(sketch, "E312.MirrorCS", {"start": v(2246.1, 2601.74) * mm, "end": v(2255.1, 2617.33) * mm});
            skLineSegment(sketch, "E313.MirrorCS", {"start": v(2527.8, 2129.65) * mm, "end": v(2536.8, 2145.24) * mm});
            skLineSegment(sketch, "E314.MirrorCS", {"start": v(3441.22, 1911.77) * mm, "end": v(3285.34, 2001.76) * mm});
            skLineSegment(sketch, "E315.MirrorCS", {"start": v(3206.64, -559.34) * mm, "end": v(3206.64, -577.34) * mm});
            skLineSegment(sketch, "E316.MirrorCS", {"start": v(2631.72, 2069.66) * mm, "end": v(2527.8, 2129.65) * mm});
            skLineSegment(sketch, "E317.MirrorCS", {"start": v(3047.42, 1829.66) * mm, "end": v(3056.42, 1845.25) * mm});
            skLineSegment(sketch, "E318.MirrorCS", {"start": v(2121.1, 2385.23) * mm, "end": v(2112.1, 2369.64) * mm});
            skLineSegment(sketch, "E319.MirrorCS", {"start": v(3106.64, -559.34) * mm, "end": v(3206.64, -559.34) * mm});
            skLineSegment(sketch, "E320.MirrorCS", {"start": v(3151.34, 1769.67) * mm, "end": v(3047.42, 1829.66) * mm});
            skLineSegment(sketch, "E321.MirrorCS", {"start": v(3106.64, -577.34) * mm, "end": v(3106.64, -559.34) * mm});
            skLineSegment(sketch, "E322.MirrorCS", {"start": v(3285.34, 2001.76) * mm, "end": v(3160.34, 1785.25) * mm, "construction": true});
            skLineSegment(sketch, "E323.MirrorCS", {"start": v(2151.17, 2677.33) * mm, "end": v(2142.17, 2661.74) * mm});
            skLineSegment(sketch, "E324.MirrorCS", {"start": v(2506.64, -577.34) * mm, "end": v(2506.64, -559.34) * mm});
            skLineSegment(sketch, "E325.MirrorCS", {"start": v(2505.9, 2451.75) * mm, "end": v(2514.9, 2467.34) * mm});
            skLineSegment(sketch, "E326.MirrorCS", {"start": v(2267.99, 2279.65) * mm, "end": v(2276.99, 2295.24) * mm});
            skLineSegment(sketch, "E327.MirrorCS", {"start": v(3025.53, 2151.76) * mm, "end": v(3034.53, 2167.35) * mm});
            skLineSegment(sketch, "E328.MirrorCS", {"start": v(2386.64, -559.34) * mm, "end": v(2386.64, -577.34) * mm});
            skLineSegment(sketch, "E329.MirrorCS", {"start": v(3190.41, 2077.35) * mm, "end": v(3181.41, 2061.76) * mm});
            skLineSegment(sketch, "E330.MirrorCS", {"start": v(2255.1, 2617.33) * mm, "end": v(2151.17, 2677.33) * mm});
            skLineSegment(sketch, "E331.MirrorCS", {"start": v(2536.8, 2145.24) * mm, "end": v(2380.9, 2235.24) * mm});
            skLineSegment(sketch, "E332.MirrorCS", {"start": v(1786.64, -559.34) * mm, "end": v(1786.64, -577.34) * mm});
            skLineSegment(sketch, "E333.MirrorCS", {"start": v(3294.34, 2017.35) * mm, "end": v(3190.41, 2077.35) * mm});
            skLineSegment(sketch, "E334.MirrorCS", {"start": v(1861.29, 2535.23) * mm, "end": v(1852.29, 2519.64) * mm});
            skLineSegment(sketch, "E335.MirrorCS", {"start": v(2206.64, -577.34) * mm, "end": v(2206.64, -559.34) * mm});
            skLineSegment(sketch, "E336.MirrorCS", {"start": v(2401.98, 2511.75) * mm, "end": v(2246.1, 2601.74) * mm});
            skLineSegment(sketch, "E337.MirrorCS", {"start": v(2017.17, 2445.23) * mm, "end": v(1861.29, 2535.23) * mm});
            skLineSegment(sketch, "E338.MirrorCS", {"start": v(2787.6, 1979.66) * mm, "end": v(2796.6, 1995.25) * mm});
            skLineSegment(sketch, "E339.MirrorCS", {"start": v(2661.8, 2361.75) * mm, "end": v(2505.9, 2451.75) * mm});
            skLineSegment(sketch, "E340.MirrorCS", {"start": v(2008.17, 2429.64) * mm, "end": v(2017.17, 2445.23) * mm});
            skLineSegment(sketch, "E341.MirrorCS", {"start": v(2410.98, 2527.33) * mm, "end": v(2401.98, 2511.75) * mm});
            skLineSegment(sketch, "E342.MirrorCS", {"start": v(2086.64, -559.34) * mm, "end": v(2086.64, -577.34) * mm});
            skLineSegment(sketch, "E343.MirrorCS", {"start": v(2891.53, 1919.66) * mm, "end": v(2787.6, 1979.66) * mm});
            skLineSegment(sketch, "E344.MirrorCS", {"start": v(2371.9, 2219.65) * mm, "end": v(2267.99, 2279.65) * mm});
            skLineSegment(sketch, "E345.MirrorCS", {"start": v(2112.1, 2369.64) * mm, "end": v(2008.17, 2429.64) * mm});
            skLineSegment(sketch, "E346.MirrorCS", {"start": v(2670.8, 2377.34) * mm, "end": v(2661.8, 2361.75) * mm});
            skLineSegment(sketch, "E347.MirrorCS", {"start": v(2506.64, -309.34) * mm, "end": v(2506.64, -291.34) * mm});
            skLineSegment(sketch, "E348.MirrorCS", {"start": v(3106.64, -291.34) * mm, "end": v(2986.64, -291.34) * mm});
            skLineSegment(sketch, "E349.MirrorCS", {"start": v(2386.64, -291.34) * mm, "end": v(2386.64, -309.34) * mm});
            skLineSegment(sketch, "E350.MirrorCS", {"start": v(2506.64, -291.34) * mm, "end": v(2386.64, -291.34) * mm});
            skLineSegment(sketch, "E351.MirrorCS", {"start": v(2380.9, 2235.24) * mm, "end": v(2371.9, 2219.65) * mm});
            skLineSegment(sketch, "E352.MirrorCS", {"start": v(2900.53, 1935.25) * mm, "end": v(2891.53, 1919.66) * mm});
            skLineSegment(sketch, "E353.MirrorCS", {"start": v(1786.64, -291.34) * mm, "end": v(1786.64, -309.34) * mm});
            skLineSegment(sketch, "E354.MirrorCS", {"start": v(1683.32, -559.34) * mm, "end": v(1683.32, -509.34) * mm});
            skLineSegment(sketch, "E355.MirrorCS", {"start": v(2514.9, 2467.34) * mm, "end": v(2410.98, 2527.33) * mm});
            skLineSegment(sketch, "E356.MirrorCS", {"start": v(2276.99, 2295.24) * mm, "end": v(2121.1, 2385.23) * mm});
            skLineSegment(sketch, "E357.MirrorCS", {"start": v(3034.53, 2167.35) * mm, "end": v(2930.6, 2227.34) * mm});
            skLineSegment(sketch, "E358.MirrorCS", {"start": v(2386.64, -577.34) * mm, "end": v(2506.64, -577.34) * mm});
            skLineSegment(sketch, "E359.MirrorCS", {"start": v(2765.72, 2301.75) * mm, "end": v(2774.72, 2317.34) * mm});
            skLineSegment(sketch, "E360.MirrorCS", {"start": v(1748.36, 2579.64) * mm, "end": v(1757.36, 2595.23) * mm});
            skLineSegment(sketch, "E361.MirrorCS", {"start": v(1906.64, -291.34) * mm, "end": v(1786.64, -291.34) * mm});
            skLineSegment(sketch, "E362.MirrorCS", {"start": v(2774.72, 2317.34) * mm, "end": v(2670.8, 2377.34) * mm});
            skLineSegment(sketch, "E363.MirrorCS", {"start": v(1786.64, -559.34) * mm, "end": v(1683.32, -559.34) * mm});
            skLineSegment(sketch, "E364.MirrorCS", {"start": v(1786.64, -577.34) * mm, "end": v(1906.64, -577.34) * mm});
            skLineSegment(sketch, "E365.MirrorCS", {"start": v(2921.6, 2211.76) * mm, "end": v(2765.72, 2301.75) * mm});
            skLineSegment(sketch, "E366.MirrorCS", {"start": v(1906.64, -309.34) * mm, "end": v(1906.64, -291.34) * mm});
            skLineSegment(sketch, "E367.MirrorCS", {"start": v(1852.29, 2519.64) * mm, "end": v(1748.36, 2579.64) * mm});
            skLineSegment(sketch, "E368.MirrorCS", {"start": v(2986.64, -559.34) * mm, "end": v(2986.64, -577.34) * mm});
            skLineSegment(sketch, "E369.MirrorCS", {"start": v(3056.42, 1845.25) * mm, "end": v(2900.53, 1935.25) * mm});
            skLineSegment(sketch, "E370.MirrorCS", {"start": v(2930.6, 2227.34) * mm, "end": v(2921.6, 2211.76) * mm});
            skLineSegment(sketch, "E371.MirrorCS", {"start": v(2246.1, 2601.74) * mm, "end": v(2121.1, 2385.23) * mm, "construction": true});
            skLineSegment(sketch, "E372.MirrorCS", {"start": v(2796.6, 1995.25) * mm, "end": v(2640.72, 2085.24) * mm});
            skLineSegment(sketch, "E373.MirrorCS", {"start": v(2806.64, -559.34) * mm, "end": v(2986.64, -559.34) * mm});
            skLineSegment(sketch, "E374.MirrorCS", {"start": v(2086.64, -577.34) * mm, "end": v(2206.64, -577.34) * mm});
            skLineSegment(sketch, "E375.MirrorCS", {"start": v(2206.64, -291.34) * mm, "end": v(2086.64, -291.34) * mm});
            skLineSegment(sketch, "E376.MirrorCS", {"start": v(2086.64, -291.34) * mm, "end": v(2086.64, -309.34) * mm});
            skLineSegment(sketch, "E377.MirrorCS", {"start": v(2806.64, -577.34) * mm, "end": v(2806.64, -559.34) * mm});
            skLineSegment(sketch, "E378.MirrorCS", {"start": v(1891.36, 2827.32) * mm, "end": v(1882.36, 2811.74) * mm});
            skLineSegment(sketch, "E379.MirrorCS", {"start": v(2686.64, -577.34) * mm, "end": v(2806.64, -577.34) * mm});
            skLineSegment(sketch, "E380.MirrorCS", {"start": v(1786.64, -309.34) * mm, "end": v(1663.32, -309.34) * mm});
            skLineSegment(sketch, "E381.MirrorCS", {"start": v(3314.4, 1098.42) * mm, "end": v(3296.4, 1098.42) * mm});
            skLineSegment(sketch, "E382.MirrorCS", {"start": v(2686.64, -291.34) * mm, "end": v(2686.64, -309.34) * mm});
            skLineSegment(sketch, "E383.MirrorCS", {"start": v(2806.64, -309.34) * mm, "end": v(2806.64, -291.34) * mm});
            skLineSegment(sketch, "E384.MirrorCS", {"start": v(2986.64, -291.34) * mm, "end": v(2986.64, -309.34) * mm});
            skLineSegment(sketch, "E385.MirrorCS", {"start": v(3564.4, 1698.42) * mm, "end": v(3582.4, 1698.42) * mm});
            skLineSegment(sketch, "E386.MirrorCS", {"start": v(3296.4, 1218.42) * mm, "end": v(3314.4, 1218.42) * mm});
            skLineSegment(sketch, "E387.MirrorCS", {"start": v(1906.64, -577.34) * mm, "end": v(1906.64, -559.34) * mm});
            skLineSegment(sketch, "E388.MirrorCS", {"start": v(2142.17, 2661.74) * mm, "end": v(1986.28, 2751.74) * mm});
            skLineSegment(sketch, "E389.MirrorCS", {"start": v(2986.64, -577.34) * mm, "end": v(3106.64, -577.34) * mm});
            skLineSegment(sketch, "E390.MirrorCS", {"start": v(3582.4, 1218.42) * mm, "end": v(3564.4, 1218.42) * mm});
            skLineSegment(sketch, "E391.MirrorCS", {"start": v(3314.4, 918.42) * mm, "end": v(3314.4, 1098.42) * mm});
            skLineSegment(sketch, "E392.MirrorCS", {"start": v(3296.4, 1098.42) * mm, "end": v(3296.4, 1218.42) * mm});
            skLineSegment(sketch, "E393.MirrorCS", {"start": v(2206.64, -559.34) * mm, "end": v(2386.64, -559.34) * mm});
            skLineSegment(sketch, "E394.MirrorCS", {"start": v(2086.64, -309.34) * mm, "end": v(1906.64, -309.34) * mm});
            skLineSegment(sketch, "E395.MirrorCS", {"start": v(3582.4, 1518.42) * mm, "end": v(3564.4, 1518.42) * mm});
            skLineSegment(sketch, "E396.MirrorCS", {"start": v(3181.41, 2061.76) * mm, "end": v(3025.53, 2151.76) * mm});
            skLineSegment(sketch, "E397.MirrorCS", {"start": v(3582.4, 1098.42) * mm, "end": v(3582.4, 1218.42) * mm});
            skLineSegment(sketch, "E398.MirrorCS", {"start": v(3582.4, 1398.42) * mm, "end": v(3582.4, 1518.42) * mm});
            skLineSegment(sketch, "E399.MirrorCS", {"start": v(1882.36, 2811.74) * mm, "end": v(1726.47, 2901.73) * mm});
            skLineSegment(sketch, "E400.MirrorCS", {"start": v(3564.4, 1398.42) * mm, "end": v(3582.4, 1398.42) * mm});
            skLineSegment(sketch, "E401.MirrorCS", {"start": v(2206.64, -309.34) * mm, "end": v(2206.64, -291.34) * mm});
            skLineSegment(sketch, "E402.MirrorCS", {"start": v(3582.4, 1698.42) * mm, "end": v(3582.4, 1818.42) * mm});
            skLineSegment(sketch, "E403.MirrorCS", {"start": v(3564.4, 1098.42) * mm, "end": v(3582.4, 1098.42) * mm});
            skLineSegment(sketch, "E404.MirrorCS", {"start": v(3564.4, 918.42) * mm, "end": v(3564.4, 1098.42) * mm});
            skLineSegment(sketch, "E405.MirrorCS", {"start": v(3314.4, 1218.42) * mm, "end": v(3314.4, 1398.42) * mm});
            skLineSegment(sketch, "E406.MirrorCS", {"start": v(2686.64, -309.34) * mm, "end": v(2506.64, -309.34) * mm});
            skLineSegment(sketch, "E407.MirrorCS", {"start": v(2806.64, -291.34) * mm, "end": v(2686.64, -291.34) * mm});
            skLineSegment(sketch, "E408.MirrorCS", {"start": v(1683.32, -509.34) * mm, "end": v(1603.32, -509.34) * mm});
            skLineSegment(sketch, "E409.MirrorCS", {"start": v(2986.64, -309.34) * mm, "end": v(2806.64, -309.34) * mm});
            skLineSegment(sketch, "E410.MirrorCS", {"start": v(2386.64, -309.34) * mm, "end": v(2206.64, -309.34) * mm});
            skLineSegment(sketch, "E411.MirrorCS", {"start": v(1995.28, 2767.33) * mm, "end": v(1891.36, 2827.32) * mm});
            skLineSegment(sketch, "E412.MirrorCS", {"start": v(2686.64, -559.34) * mm, "end": v(2686.64, -577.34) * mm});
            skLineSegment(sketch, "E413.MirrorCS", {"start": v(1906.64, -559.34) * mm, "end": v(2086.64, -559.34) * mm});
            skLineSegment(sketch, "E414.MirrorCS", {"start": v(1986.28, 2751.74) * mm, "end": v(1995.28, 2767.33) * mm});
            skLineSegment(sketch, "E415.MirrorCS", {"start": v(2506.64, -559.34) * mm, "end": v(2686.64, -559.34) * mm});
            skLineSegment(sketch, "E416.MirrorCS", {"start": v(3564.4, 1518.42) * mm, "end": v(3564.4, 1698.42) * mm});
            skLineSegment(sketch, "E417.MirrorCS", {"start": v(3564.4, 1218.42) * mm, "end": v(3564.4, 1398.42) * mm});
            skLineSegment(sketch, "E418.MirrorCS", {"start": v(3296.4, 1398.42) * mm, "end": v(3296.4, 1518.42) * mm});
            skLineSegment(sketch, "E419.MirrorCS", {"start": v(3296.4, 1518.42) * mm, "end": v(3314.4, 1518.42) * mm});
            skLineSegment(sketch, "E420.MirrorCS", {"start": v(3314.4, 1398.42) * mm, "end": v(3296.4, 1398.42) * mm});
            skLineSegment(sketch, "E421.MirrorCS", {"start": v(3160.34, 1785.25) * mm, "end": v(3314.4, 1696.31) * mm});
            skLineSegment(sketch, "E422.MirrorCS", {"start": v(3314.4, 1518.42) * mm, "end": v(3314.4, 1696.31) * mm});
            skLineSegment(sketch, "E423.MirrorCS", {"start": v(1757.36, 2595.23) * mm, "end": v(1603.3, 2684.17) * mm});
            skPoint(sketch, "E424.MirrorP", {"position": v(3564.4, 558.42) * mm});
            skPoint(sketch, "E425.MirrorP", {"position": v(3314.4, 558.42) * mm});
            skLineSegment(sketch, "E426", {"start": v(55.3, 1769.67) * mm, "end": v(-107.77, 1675.53) * mm, "construction": true});
            skLineSegment(sketch, "E427", {"start": v(-89.77, 1518.42) * mm, "end": v(-89.77, 1706.7) * mm, "construction": true});
            skPoint(sketch, "E428", {"position": v(-89.77, 1685.92) * mm});
            skPoint(sketch, "E429", {"position": v(-89.77, 1640.92) * mm});
            skLineSegment(sketch, "E430", {"start": v(1458.27, 2579.64) * mm, "end": v(1621.32, 2673.77) * mm, "construction": true});
            skLineSegment(sketch, "E431", {"start": v(1748.36, 2579.64) * mm, "end": v(1585.32, 2673.77) * mm, "construction": true});
            skPoint(sketch, "E432", {"position": v(1603.32, 2663.38) * mm});
            skLineSegment(sketch, "E433", {"start": v(1575.09, 2977.32) * mm, "end": v(1603.32, 2993.62) * mm, "construction": true});
            skLineSegment(sketch, "E434", {"start": v(1631.55, 2977.32) * mm, "end": v(1603.32, 2993.62) * mm, "construction": true});
            skLineSegment(sketch, "E435", {"start": v(-347.51, 1867.36) * mm, "end": v(-375.77, 1851.04) * mm, "construction": true});
            skLineSegment(sketch, "E436", {"start": v(-375.77, 1851.04) * mm, "end": v(-375.77, 1818.42) * mm, "construction": true});
            skLineSegment(sketch, "E437", {"start": v(-120, -577.34) * mm, "end": v(-375.77, -577.34) * mm, "construction": true});
            skLineSegment(sketch, "E438", {"start": v(1130.23, -291.34) * mm, "end": v(1130.23, 392.9) * mm, "construction": true});
            skLineSegment(sketch, "E439", {"start": v(2076.4, -291.34) * mm, "end": v(2076.4, 2148.66) * mm, "construction": true});
            skLineSegment(sketch, "E440", {"start": v(3047.42, 1829.66) * mm, "end": v(1748.36, 2579.64) * mm, "construction": true});
            skLineSegment(sketch, "E441", {"start": v(2076.4, 2148.66) * mm, "end": v(2494.88, 2148.66) * mm, "construction": true});
            skLineSegment(sketch, "E442", {"start": v(2494.88, 2148.66) * mm, "end": v(2494.88, -291.34) * mm, "construction": true});
            skLineSegment(sketch, "E443", {"start": v(3314.4, 1696.31) * mm, "end": v(3564.4, 1840.65) * mm, "construction": true});
            skLineSegment(sketch, "E444", {"start": v(3296.4, -291.34) * mm, "end": v(3296.4, -577.34) * mm, "construction": true});
            skLineSegment(sketch, "E445", {"start": v(1603.33, 2917.65) * mm, "end": v(1603.33, 2684.17) * mm, "construction": true});
            skLineSegment(sketch, "E446", {"start": v(1603.33, 2800.91) * mm, "end": v(3439.4, 1768.48) * mm, "construction": true});
            skLineSegment(sketch, "E447", {"start": v(1603.32, -509.34) * mm, "end": v(1603.32, -327.34) * mm, "construction": true});
            skLineSegment(sketch, "E448", {"start": v(1603.32, -418.34) * mm, "end": v(3296.4, -418.34) * mm, "construction": true});
            skLineSegment(sketch, "E449", {"start": v(3439.4, 1768.48) * mm, "end": v(3439.4, -509.34) * mm, "construction": true});
            skSolve(sketch);
        }
        {
            var Q0;
            Q0=makeQuery(id+"F0.imprint","IMPRINT",FACE,{"disambiguationData":[TD([[makeQuery(id+"F0.imprint","IMPRINT",EDGE,{"derivedFrom":sQuery(id+"F0.wireOp",EDGE,"E0")}),-1.0]])]});
            extrude(context, id + "F1", {"entities" : qUnion([Q0]), "depth" : 4800 * mm});
        }
    });
